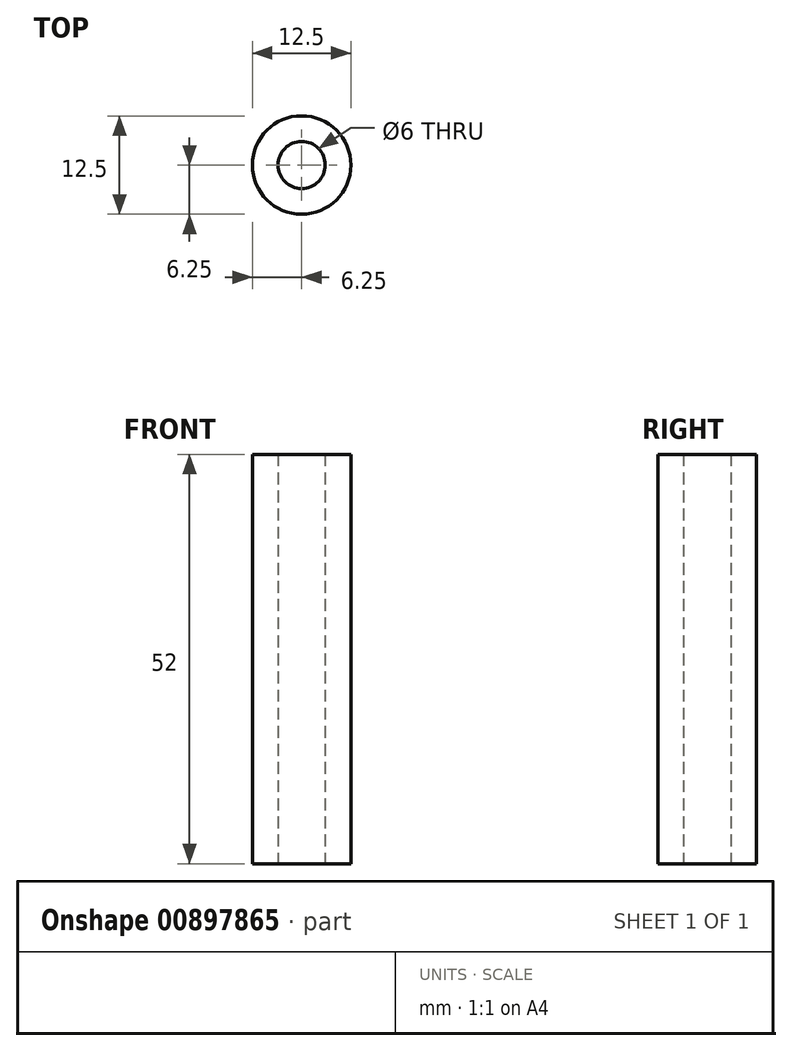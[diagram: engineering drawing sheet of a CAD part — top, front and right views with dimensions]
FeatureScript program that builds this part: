
annotation { "Feature Type Name" : "Feature", "Feature Type Description" : "" }
export const myFeature = defineFeature(function(context is Context, id is Id, definition is map)
    precondition{}
    {
        {
            var Q0;
            Q0=qCreatedBy(makeId("Top.planeOp"),FACE);
            var sketch = newSketch(context, id + "F0", { "sketchPlane" : qUnion([Q0])});
            skCircle(sketch, "E0", {"center": v(0, 0) * mm, "radius": 6.25 * mm});
            skCircle(sketch, "E1", {"center": v(0, 0) * mm, "radius": 3 * mm});
            skSolve(sketch);
        }
        {
            var Q0;
            Q0 = qSketchRegion(id + "F0", true);
            extrude(context, id + "F1", {"entities" : qUnion([Q0]), "depth" : 52 * mm, "offsetDistance" : 25 * mm});
        }
    });
